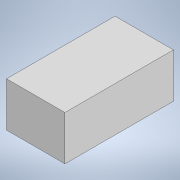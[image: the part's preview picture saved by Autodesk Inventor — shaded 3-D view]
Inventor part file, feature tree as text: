
AUTODESK INVENTOR PART (.ipt)
format: ipt  version: 2021 (Build 250183000, 183)  size: 86,016 bytes
history: native  units: mm
features: other x1, extrude x1, sketch x1
ambient origin geometry x8: Origin, YZ Plane, XZ Plane, XY Plane, X Axis, Y Axis, Z Axis, Center Point
bodies: Body1 (feature_tree)
feature tree (3):
  other  "Sólido1"
  extrude  "Extrusión1"  Depth=39.0mm
  sketch  "Boceto1"  dims[d3=21.0mm d4=39.0mm d5=16.0mm d6=0.0mm]
